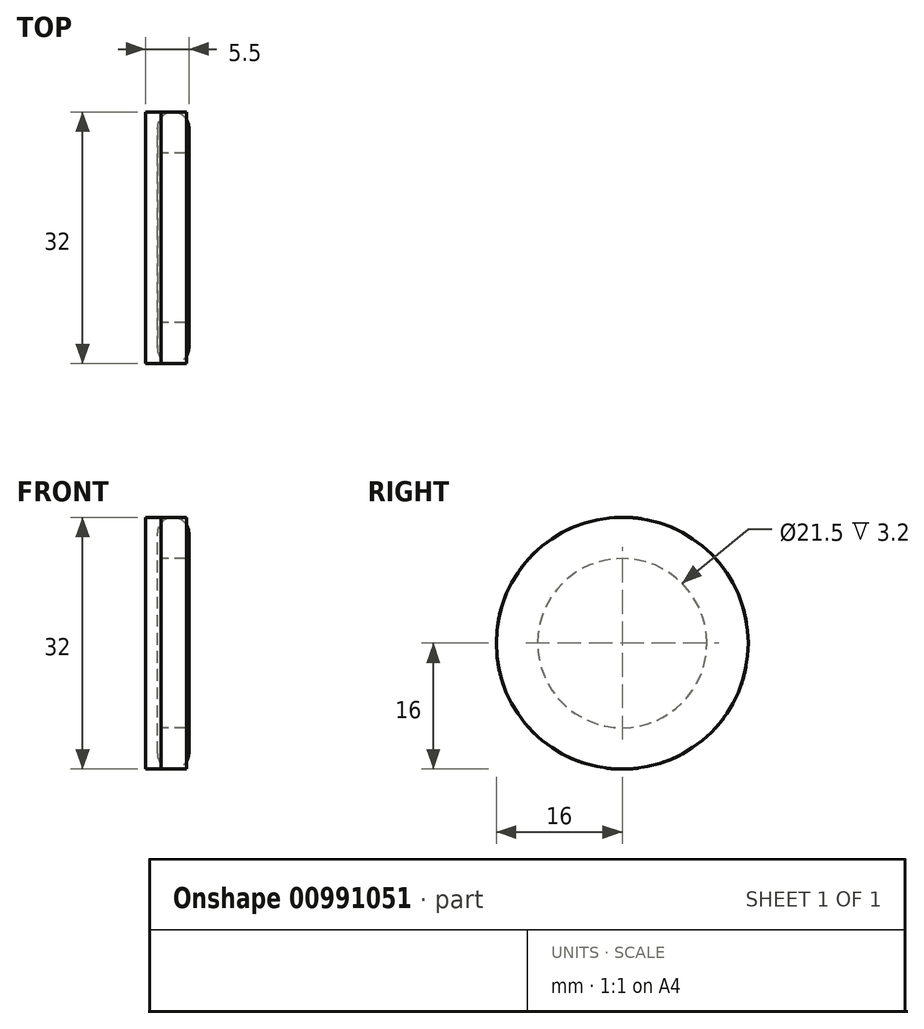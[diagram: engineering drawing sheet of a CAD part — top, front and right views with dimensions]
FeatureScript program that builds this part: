
annotation { "Feature Type Name" : "Feature", "Feature Type Description" : "" }
export const myFeature = defineFeature(function(context is Context, id is Id, definition is map)
    precondition{}
    {
        {
            var Q0;
            Q0=qCreatedBy(makeId("Right.planeOp"),FACE);
            var sketch = newSketch(context, id + "F0", { "sketchPlane" : qUnion([Q0])});
            skCircle(sketch, "E0", {"center": v(0, 0) * mm, "radius": 11 * mm});
            skSolve(sketch);
        }
        {
            var Q0;
            Q0=makeQuery(id+"F0.imprint","IMPRINT",FACE,{"disambiguationData":[TD([[makeQuery(id+"F0.imprint","IMPRINT",EDGE,{"derivedFrom":sQuery(id+"F0.wireOp",EDGE,"E0")}),1.0]])]});
            extrude(context, id + "F1", {"entities" : qUnion([Q0]), "depth" : 1 * mm, "offsetDistance" : 25 * mm});
        }
        {
            var Q0;
            Q0=makeQuery(id+"F1.opExtrude","CAP_FACE",FACE,{"disambiguationData":[OSD([sQuery(id+"F0.wireOp",EDGE,"E0")])],"isStart":false});
            var sketch = newSketch(context, id + "F2", { "sketchPlane" : qUnion([Q0])});
            skCircle(sketch, "E1", {"center": v(-6.28, 7.07) * mm, "radius": 1 * mm});
            skSolve(sketch);
        }
        {
            var Q0;
            Q0=makeQuery(id+"F2.imprint","IMPRINT",FACE,{"disambiguationData":[TD([[makeQuery(id+"F2.imprint","IMPRINT",EDGE,{"derivedFrom":sQuery(id+"F2.wireOp",EDGE,"E1")}),1.0]])]});
            var Q1;
            Q1=sQuery(id+"F2.wireOp",EDGE,"E1");
            extrude(context, id + "F3", {"entities" : qUnion([Q0]), "operationType" : NewBodyOperationType.ADD, "surfaceEntities" : qUnion([Q1]), "depth" : 2 * mm, "offsetDistance" : 25 * mm});
        }
        {
            var Q0;
            Q0=makeQuery(id+"F3.opExtrude","CAP_EDGE",EDGE,{"disambiguationData":[OSD([sQuery(id+"F2.wireOp",EDGE,"E1")])],"isStart":false});
            fillet(context, id + "F4", {"entities" : qUnion([Q0]), "radius" : 1 * mm, "tangentPropagation" : true, "allowEdgeOverflow" : false});
        }
        {
            var Q0;
            Q0=qCreatedBy(makeId("Right.planeOp"),FACE);
            var sketch = newSketch(context, id + "F5", { "sketchPlane" : qUnion([Q0])});
            skCircle(sketch, "E2", {"center": v(0, 0) * mm, "radius": 16 * mm});
            skSolve(sketch);
        }
        {
            var Q0;
            Q0 = qSketchRegion(id + "F5", true);
            extrude(context, id + "F6", {"entities" : qUnion([Q0]), "depth" : 3.5 * mm, "offsetDistance" : 25 * mm});
        }
        {
            var Q0;
            Q0=makeQuery(id+"F6.opExtrude","CAP_FACE",FACE,{"disambiguationData":[OSD([sQuery(id+"F5.wireOp",EDGE,"E2")])],"isStart":true});
            extrude(context, id + "F7", {"entities" : qUnion([Q0]), "operationType" : NewBodyOperationType.ADD, "depth" : 0.5 * mm, "offsetDistance" : 25 * mm});
        }
        {
            var Q0;
            Q0=makeQuery(id+"F6.opExtrude","CAP_EDGE",EDGE,{"disambiguationData":[OSD([sQuery(id+"F5.wireOp",EDGE,"E2")])],"isStart":false});
            var Q1;
            Q1=makeQuery(id+"F7.opExtrude","CAP_EDGE",EDGE,{"disambiguationData":[OSD([sQuery(id+"F5.wireOp",EDGE,"E2")])],"isStart":false});
            fillet(context, id + "F8", {"entities" : qUnion([Q0, Q1]), "radius" : 2 * mm, "tangentPropagation" : true, "allowEdgeOverflow" : false});
        }
        {
            var Q0;
            Q0 = qSketchRegion(id + "F5", true);
            extrude(context, id + "F9", {"entities" : qUnion([Q0]), "oppositeDirection" : true, "depth" : 2 * mm, "offsetDistance" : 25 * mm});
        }
        {
            var Q0;
            Q0=makeQuery(id+"F5.imprint","IMPRINT",FACE,{"disambiguationData":[TD([[makeQuery(id+"F5.imprint","IMPRINT",EDGE,{"derivedFrom":sQuery(id+"F5.wireOp",EDGE,"E2")}),1.0]])]});
            extrude(context, id + "F10", {"entities" : qUnion([Q0]), "depth" : 25 * mm, "offsetDistance" : 25 * mm});
        }
        {
            var Q0;
            Q0=makeQuery(id+"F10.opExtrude","SWEPT_BODY",BODY,{"disambiguationData":[OSD([sQuery(id+"F5.wireOp",EDGE,"E2")])]});
            deleteBodies(context, id + "F11", {"entities" : qUnion([Q0])});
        }
        {
            var Q0;
            Q0=makeQuery(id+"F5.imprint","IMPRINT",FACE,{"disambiguationData":[TD([[makeQuery(id+"F5.imprint","IMPRINT",EDGE,{"derivedFrom":sQuery(id+"F5.wireOp",EDGE,"E2")}),1.0]])]});
            var sketch = newSketch(context, id + "F12", { "sketchPlane" : qUnion([Q0])});
            skCircle(sketch, "E3", {"center": v(0, 0) * mm, "radius": 10.75 * mm});
            skCircle(sketch, "E4.0", {"center": v(0, 0) * mm, "radius": 16 * mm});
            skSolve(sketch);
        }
        {
            var Q0;
            Q0=makeQuery(id+"F12.imprint","IMPRINT",FACE,{"disambiguationData":[TD([[makeQuery(id+"F12.imprint","IMPRINT",EDGE,{"derivedFrom":sQuery(id+"F12.wireOp",EDGE,"E3")}),-1.0]])]});
            extrude(context, id + "F13", {"entities" : qUnion([Q0]), "depth" : 3.2 * mm, "offsetDistance" : 25 * mm});
        }
    });
